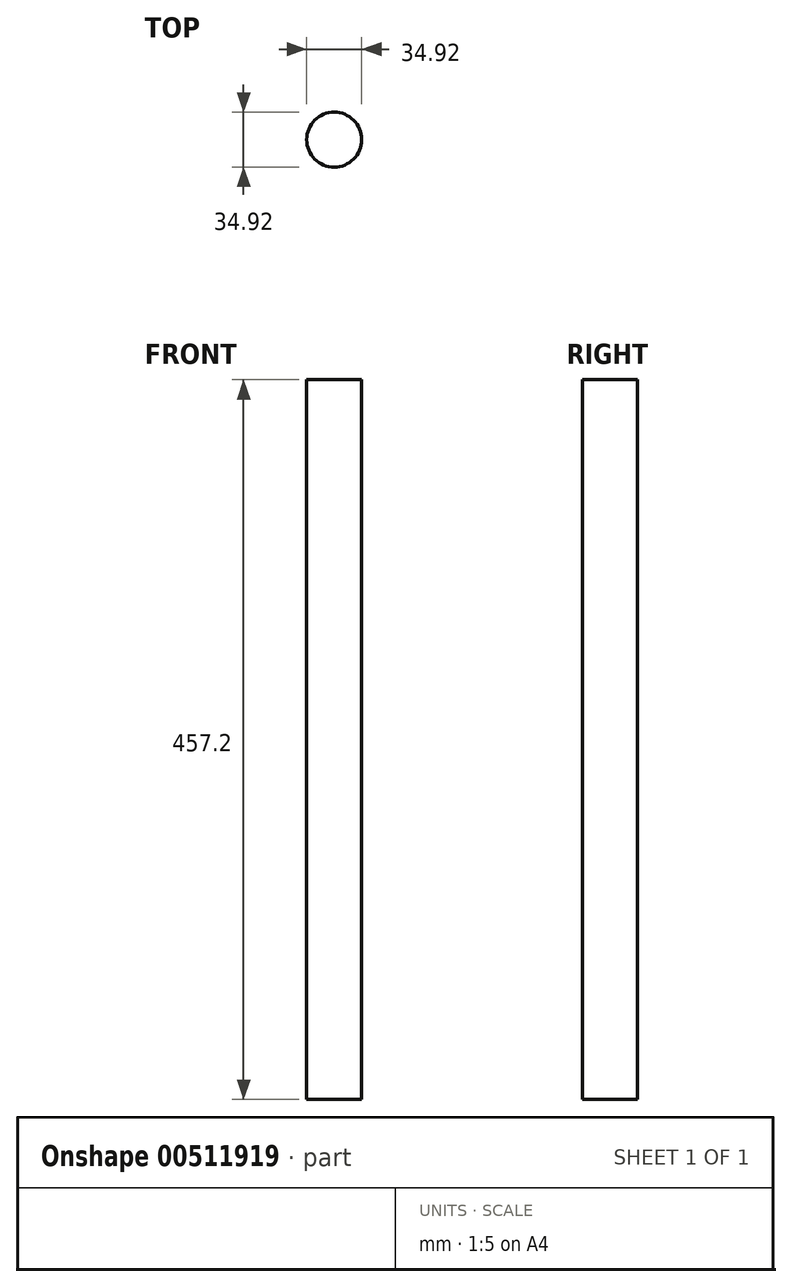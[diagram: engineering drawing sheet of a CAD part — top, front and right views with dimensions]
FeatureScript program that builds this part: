
annotation { "Feature Type Name" : "Feature", "Feature Type Description" : "" }
export const myFeature = defineFeature(function(context is Context, id is Id, definition is map)
    precondition{}
    {
        {
            var Q0;
            Q0=qCreatedBy(makeId("Top.planeOp"),FACE);
            var sketch = newSketch(context, id + "F0", { "sketchPlane" : qUnion([Q0])});
            skCircle(sketch, "E0", {"center": v(0, 0) * mm, "radius": 17.46 * mm});
            skSolve(sketch);
        }
        {
            var Q0;
            Q0 = qSketchRegion(id + "F0", true);
            extrude(context, id + "F1", {"entities" : qUnion([Q0]), "depth" : 457.2 * mm, "offsetDistance" : 25.4 * mm});
        }
    });
